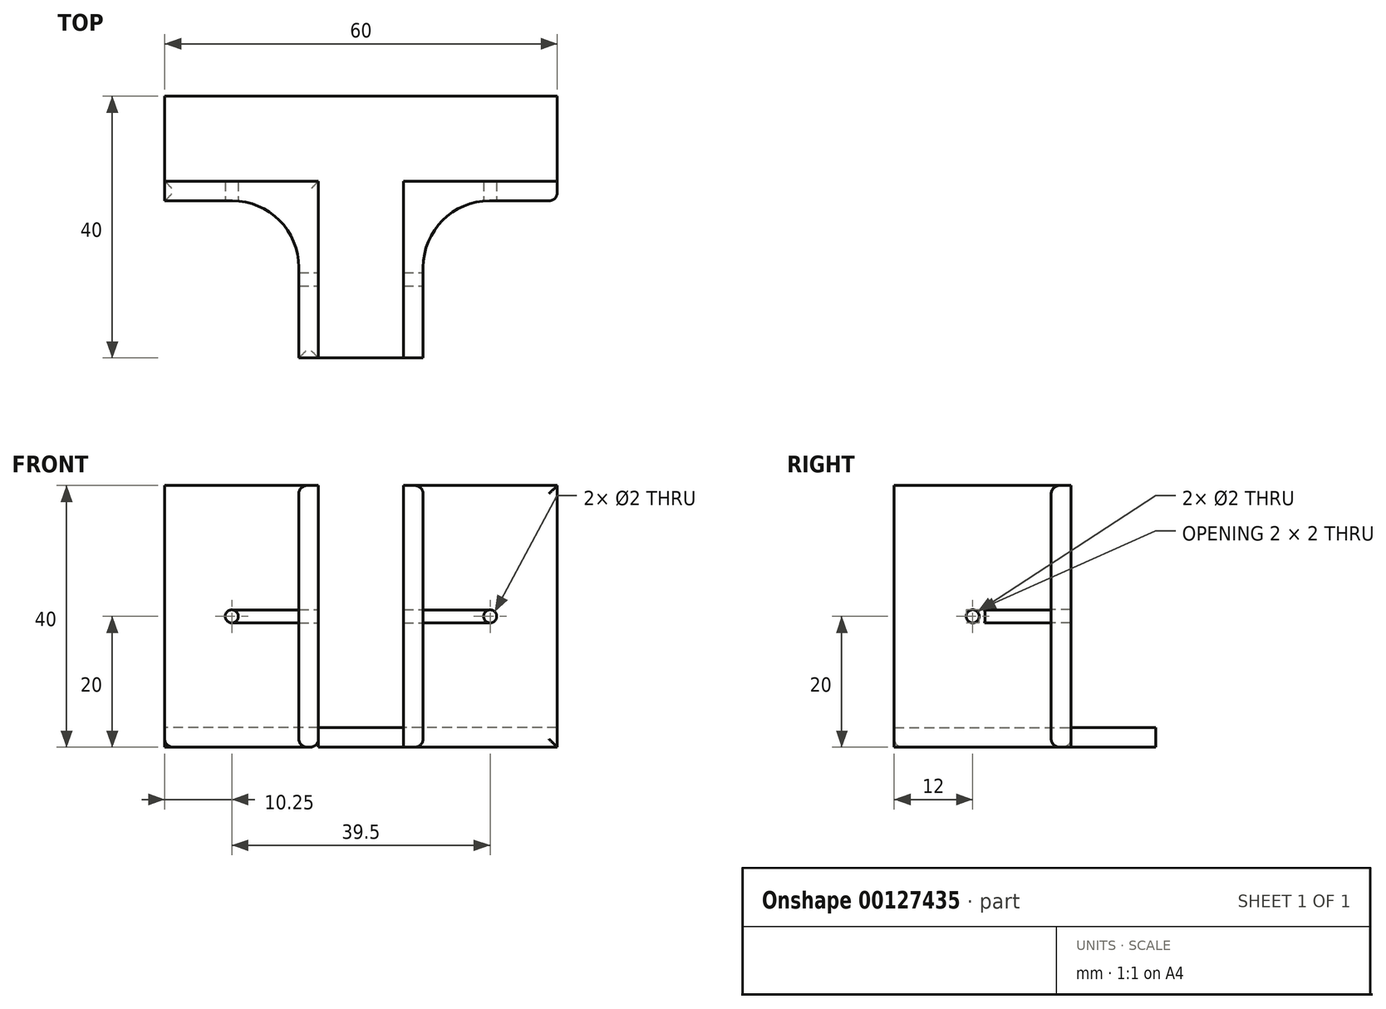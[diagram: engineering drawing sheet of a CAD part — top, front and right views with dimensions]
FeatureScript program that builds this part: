
annotation { "Feature Type Name" : "Feature", "Feature Type Description" : "" }
export const myFeature = defineFeature(function(context is Context, id is Id, definition is map)
    precondition{}
    {
        {
            var Q0;
            Q0=qCreatedBy(makeId("Top.planeOp"),FACE);
            var sketch = newSketch(context, id + "F0", { "sketchPlane" : qUnion([Q0])});
            skLineSegment(sketch, "E0.bottom", {"start": v(30, 6.5) * mm, "end": v(-30, 6.5) * mm});
            skLineSegment(sketch, "E0.top", {"start": v(30, -6.5) * mm, "end": v(6.5, -6.5) * mm});
            skLineSegment(sketch, "E0.left", {"start": v(30, 6.5) * mm, "end": v(30, -6.5) * mm});
            skLineSegment(sketch, "E0.right", {"start": v(-30, 6.5) * mm, "end": v(-30, -6.5) * mm});
            skPoint(sketch, "E0.middle", {"position": v(0, 0) * mm});
            skLineSegment(sketch, "E1.bottom", {"start": v(6.5, -33.5) * mm, "end": v(-6.5, -33.5) * mm});
            skLineSegment(sketch, "E1.left", {"start": v(6.5, -33.5) * mm, "end": v(6.5, -6.5) * mm});
            skLineSegment(sketch, "E1.right", {"start": v(-6.5, -33.5) * mm, "end": v(-6.5, -6.5) * mm});
            skPoint(sketch, "E2.orphan", {"position": v(-6.5, 33.5) * mm});
            skPoint(sketch, "E3.orphan", {"position": v(6.5, 33.5) * mm});
            skLineSegment(sketch, "E4.trimOffspring", {"start": v(-6.5, -6.5) * mm, "end": v(-30, -6.5) * mm});
            skLineSegment(sketch, "E5.bottom", {"start": v(-30, 6.5) * mm, "end": v(30, 6.5) * mm});
            skLineSegment(sketch, "E5.top", {"start": v(-30, 9.5) * mm, "end": v(30, 9.5) * mm});
            skLineSegment(sketch, "E5.left", {"start": v(-30, 6.5) * mm, "end": v(-30, 9.5) * mm});
            skLineSegment(sketch, "E5.right", {"start": v(30, 6.5) * mm, "end": v(30, 9.5) * mm});
            skLineSegment(sketch, "E6", {"start": v(-30, -6.5) * mm, "end": v(-30, -9.5) * mm});
            skLineSegment(sketch, "E7", {"start": v(-30, -9.5) * mm, "end": v(-9.5, -9.5) * mm});
            skLineSegment(sketch, "E8", {"start": v(-9.5, -9.5) * mm, "end": v(-9.5, -33.5) * mm});
            skLineSegment(sketch, "E9", {"start": v(-9.5, -33.5) * mm, "end": v(-6.5, -33.5) * mm});
            skLineSegment(sketch, "E10", {"start": v(6.5, -33.5) * mm, "end": v(9.5, -33.5) * mm});
            skLineSegment(sketch, "E11", {"start": v(9.5, -33.5) * mm, "end": v(9.5, -9.5) * mm});
            skLineSegment(sketch, "E12", {"start": v(9.5, -9.5) * mm, "end": v(30, -9.5) * mm});
            skLineSegment(sketch, "E13", {"start": v(30, -9.5) * mm, "end": v(30, -6.5) * mm});
            skSolve(sketch);
        }
        {
            var Q0;
            Q0=makeQuery(id+"F0.imprint","IMPRINT",FACE,{"disambiguationData":[TD([[makeQuery(id+"F0.imprint","IMPRINT",EDGE,{"derivedFrom":sQuery(id+"F0.wireOp",EDGE,"E1.right")}),1.0]])]});
            var Q1;
            Q1=makeQuery(id+"F0.imprint","IMPRINT",FACE,{"disambiguationData":[TD([[makeQuery(id+"F0.imprint","IMPRINT",EDGE,{"derivedFrom":sQuery(id+"F0.wireOp",EDGE,"E0.top")}),1.0]])]});
            extrude(context, id + "F1", {"entities" : qUnion([Q0, Q1]), "depth" : 40 * mm});
        }
        {
            var Q0;
            Q0=makeQuery(id+"F0.imprint","IMPRINT",FACE,{"disambiguationData":[TD([[makeQuery(id+"F0.imprint","IMPRINT",EDGE,{"derivedFrom":sQuery(id+"F0.wireOp",EDGE,"E0.top")}),-1.0]])]});
            extrude(context, id + "F2", {"entities" : qUnion([Q0]), "depth" : 3 * mm});
        }
        {
            var Q0;
            Q0=makeQuery(id+"F1.opExtrude","SWEPT_FACE",FACE,{"disambiguationData":[OSD([sQuery(id+"F0.wireOp",EDGE,"E11")])]});
            var sketch = newSketch(context, id + "F3", { "sketchPlane" : qUnion([Q0])});
            skCircle(sketch, "E14", {"center": v(-21.5, 20) * mm, "radius": 1 * mm});
            skPoint(sketch, "E14.centerSnap0", {"position": v(-33.5, 20) * mm});
            skPoint(sketch, "E14.centerSnap1", {"position": v(-21.5, 40) * mm});
            skSolve(sketch);
        }
        {
            var Q0;
            Q0=makeQuery(id+"F1.opExtrude","SWEPT_FACE",FACE,{"disambiguationData":[OSD([sQuery(id+"F0.wireOp",EDGE,"E12")])]});
            var sketch = newSketch(context, id + "F4", { "sketchPlane" : qUnion([Q0])});
            skCircle(sketch, "E15", {"center": v(19.75, 20) * mm, "radius": 1 * mm});
            skPoint(sketch, "E15.centerSnap0", {"position": v(30, 20) * mm});
            skPoint(sketch, "E15.centerSnap1", {"position": v(19.75, 40) * mm});
            skSolve(sketch);
        }
        {
            var Q0;
            Q0=makeQuery(id+"F4.imprint","IMPRINT",FACE,{"disambiguationData":[TD([[makeQuery(id+"F4.imprint","IMPRINT",EDGE,{"derivedFrom":sQuery(id+"F4.wireOp",EDGE,"E15")}),1.0]])]});
            extrude(context, id + "F5", {"entities" : qUnion([Q0]), "operationType" : NewBodyOperationType.REMOVE, "oppositeDirection" : true, "depth" : 25.4 * mm});
        }
        {
            var Q0;
            Q0=makeQuery(id+"F1.opExtrude","SWEPT_FACE",FACE,{"disambiguationData":[OSD([sQuery(id+"F0.wireOp",EDGE,"E7")])]});
            var sketch = newSketch(context, id + "F6", { "sketchPlane" : qUnion([Q0])});
            skCircle(sketch, "E16", {"center": v(-19.75, 20) * mm, "radius": 1 * mm});
            skPoint(sketch, "E16.centerSnap0", {"position": v(-30, 20) * mm});
            skPoint(sketch, "E16.centerSnap1", {"position": v(-19.75, 40) * mm});
            skSolve(sketch);
        }
        {
            var Q0;
            Q0=makeQuery(id+"F6.imprint","IMPRINT",FACE,{"disambiguationData":[TD([[makeQuery(id+"F6.imprint","IMPRINT",EDGE,{"derivedFrom":sQuery(id+"F6.wireOp",EDGE,"E16")}),1.0]])]});
            extrude(context, id + "F7", {"entities" : qUnion([Q0]), "operationType" : NewBodyOperationType.REMOVE, "oppositeDirection" : true, "depth" : 25.4 * mm});
        }
        {
            var Q0;
            Q0=makeQuery(id+"F3.imprint","IMPRINT",FACE,{"disambiguationData":[TD([[makeQuery(id+"F3.imprint","IMPRINT",EDGE,{"derivedFrom":sQuery(id+"F3.wireOp",EDGE,"E14")}),1.0]])]});
            extrude(context, id + "F8", {"entities" : qUnion([Q0]), "operationType" : NewBodyOperationType.REMOVE, "oppositeDirection" : true, "depth" : 25.4 * mm});
        }
        {
            var Q0;
            Q0=makeQuery(id+"F1.opExtrude","SWEPT_EDGE",EDGE,{"disambiguationData":[OSD([sQuery(id+"F0.wireOp",EDGE,"E11"),sQuery(id+"F0.wireOp",EDGE,"E12")])]});
            var Q1;
            Q1=makeQuery(id+"F1.opExtrude","SWEPT_EDGE",EDGE,{"disambiguationData":[OSD([sQuery(id+"F0.wireOp",EDGE,"E7"),sQuery(id+"F0.wireOp",EDGE,"E8")])]});
            fillet(context, id + "F9", {"entities" : qUnion([Q0, Q1]), "radius" : 10.16 * mm, "tangentPropagation" : true, "allowEdgeOverflow" : false});
        }
        {
            var Q0;
            Q0=makeQuery(id+"F1.opExtrude","CAP_EDGE",EDGE,{"disambiguationData":[OSD([sQuery(id+"F0.wireOp",EDGE,"E5.top")])],"isStart":false});
            var Q1;
            Q1=makeQuery(id+"F1.opExtrude","SWEPT_EDGE",EDGE,{"disambiguationData":[OSD([sQuery(id+"F0.wireOp",EDGE,"E12"),sQuery(id+"F0.wireOp",EDGE,"E13")])]});
            var Q2;
            Q2=makeQuery(id+"F1.opExtrude","CAP_EDGE",EDGE,{"disambiguationData":[OSD([sQuery(id+"F0.wireOp",EDGE,"E12")])],"isStart":false});
            var Q3;
            {var subQ0=sQuery(id+"F0.wireOp",EDGE,"E12");var subQ1=sQuery(id+"F0.wireOp",EDGE,"E11");Q3=makeQuery(id+"F9.opFillet","BLEND_EDGE",EDGE,{"blendedFrom":[makeQuery(id+"F1.opExtrude","SWEPT_EDGE",EDGE,{"disambiguationData":[OSD([subQ1,subQ0])]}),makeQuery(id+"F1.opExtrude","CAP_FACE",FACE,{"disambiguationData":[OSD([sQuery(id+"F0.wireOp",EDGE,"E0.top"),sQuery(id+"F0.wireOp",EDGE,"E1.left"),sQuery(id+"F0.wireOp",EDGE,"E10"),subQ1,subQ0,sQuery(id+"F0.wireOp",EDGE,"E13")])],"isStart":false})],"blendedInto":[makeQuery(id+"F1.opExtrude","CAP_FACE",FACE,{"disambiguationData":[OSD([sQuery(id+"F0.wireOp",EDGE,"E0.top"),sQuery(id+"F0.wireOp",EDGE,"E1.left"),sQuery(id+"F0.wireOp",EDGE,"E10"),subQ1,subQ0,sQuery(id+"F0.wireOp",EDGE,"E13")])],"isStart":false})]});}
            var Q4;
            Q4=makeQuery(id+"F1.opExtrude","CAP_EDGE",EDGE,{"disambiguationData":[OSD([sQuery(id+"F0.wireOp",EDGE,"E11")])],"isStart":false});
            var Q5;
            Q5=makeQuery(id+"F1.opExtrude","CAP_EDGE",EDGE,{"disambiguationData":[OSD([sQuery(id+"F0.wireOp",EDGE,"E8")])],"isStart":false});
            var Q6;
            {var subQ0=sQuery(id+"F0.wireOp",EDGE,"E8");var subQ1=sQuery(id+"F0.wireOp",EDGE,"E7");Q6=makeQuery(id+"F9.opFillet","BLEND_EDGE",EDGE,{"blendedFrom":[makeQuery(id+"F1.opExtrude","SWEPT_EDGE",EDGE,{"disambiguationData":[OSD([subQ1,subQ0])]}),makeQuery(id+"F1.opExtrude","CAP_FACE",FACE,{"disambiguationData":[OSD([sQuery(id+"F0.wireOp",EDGE,"E1.right"),sQuery(id+"F0.wireOp",EDGE,"E4.trimOffspring"),sQuery(id+"F0.wireOp",EDGE,"E6"),subQ1,subQ0,sQuery(id+"F0.wireOp",EDGE,"E9")])],"isStart":false})],"blendedInto":[makeQuery(id+"F1.opExtrude","CAP_FACE",FACE,{"disambiguationData":[OSD([sQuery(id+"F0.wireOp",EDGE,"E1.right"),sQuery(id+"F0.wireOp",EDGE,"E4.trimOffspring"),sQuery(id+"F0.wireOp",EDGE,"E6"),subQ1,subQ0,sQuery(id+"F0.wireOp",EDGE,"E9")])],"isStart":false})]});}
            var Q7;
            Q7=makeQuery(id+"F1.opExtrude","CAP_EDGE",EDGE,{"disambiguationData":[OSD([sQuery(id+"F0.wireOp",EDGE,"E7")])],"isStart":false});
            var Q8;
            Q8=makeQuery(id+"F1.opExtrude","CAP_EDGE",EDGE,{"disambiguationData":[OSD([sQuery(id+"F0.wireOp",EDGE,"E5.top")])],"isStart":true});
            var Q9;
            Q9=makeQuery(id+"F1.opExtrude","CAP_EDGE",EDGE,{"disambiguationData":[OSD([sQuery(id+"F0.wireOp",EDGE,"E7")])],"isStart":true});
            var Q10;
            Q10=makeQuery(id+"F1.opExtrude","CAP_FACE",FACE,{"disambiguationData":[OSD([sQuery(id+"F0.wireOp",EDGE,"E1.right"),sQuery(id+"F0.wireOp",EDGE,"E4.trimOffspring"),sQuery(id+"F0.wireOp",EDGE,"E6"),sQuery(id+"F0.wireOp",EDGE,"E7"),sQuery(id+"F0.wireOp",EDGE,"E8"),sQuery(id+"F0.wireOp",EDGE,"E9")])],"isStart":true});
            var Q11;
            Q11=makeQuery(id+"F1.opExtrude","CAP_EDGE",EDGE,{"disambiguationData":[OSD([sQuery(id+"F0.wireOp",EDGE,"E12")])],"isStart":true});
            fillet(context, id + "F10", {"entities" : qUnion([Q0, Q1, Q2, Q3, Q4, Q5, Q6, Q7, Q8, Q9, Q10, Q11]), "radius" : 1.27 * mm, "tangentPropagation" : true, "allowEdgeOverflow" : false});
        }
    });
